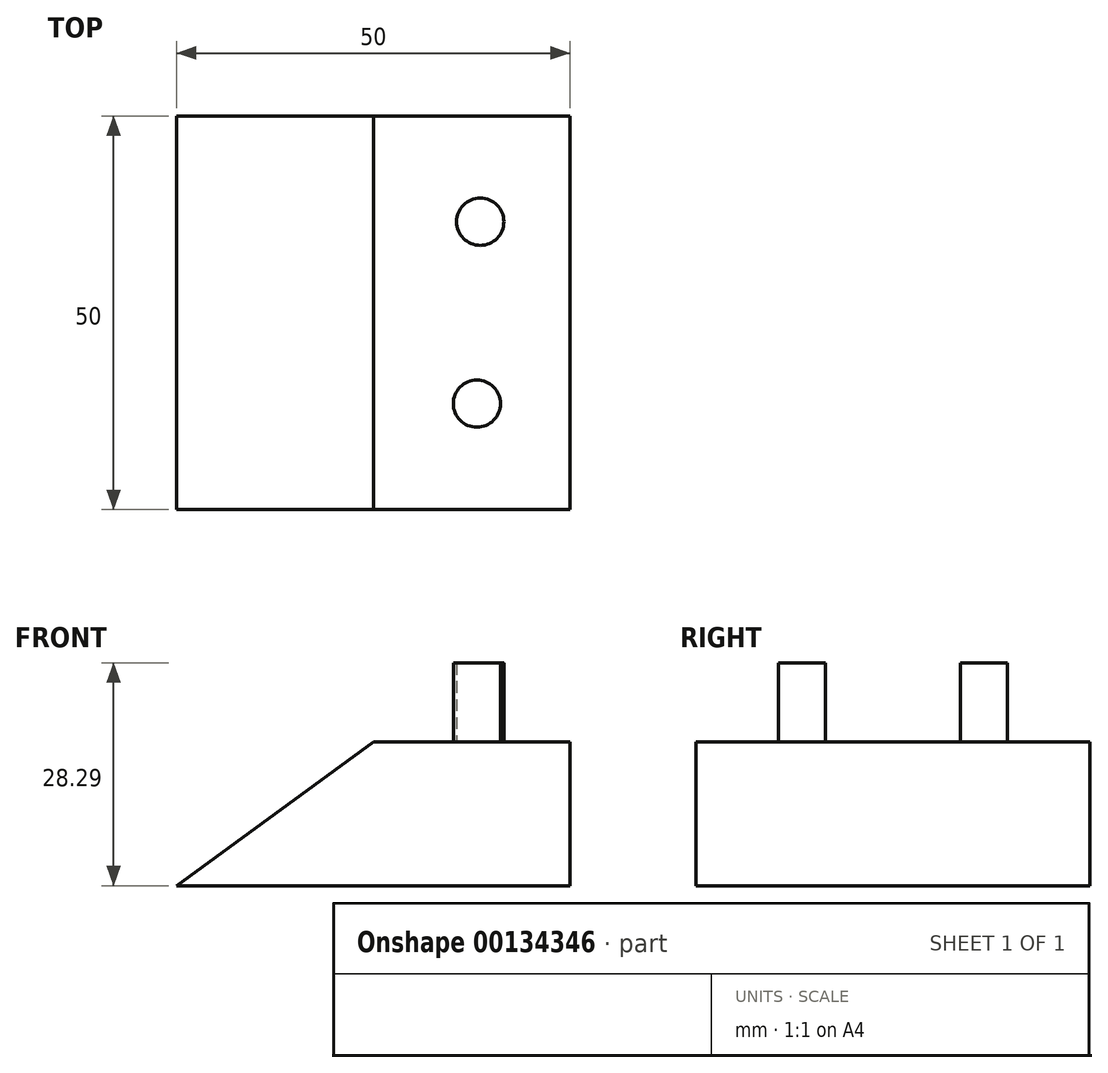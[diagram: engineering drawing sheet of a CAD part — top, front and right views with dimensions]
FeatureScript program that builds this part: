
annotation { "Feature Type Name" : "Feature", "Feature Type Description" : "" }
export const myFeature = defineFeature(function(context is Context, id is Id, definition is map)
    precondition{}
    {
        {
            var Q0;
            Q0=qCreatedBy(makeId("Front.planeOp"),FACE);
            var sketch = newSketch(context, id + "F0", { "sketchPlane" : qUnion([Q0])});
            skLineSegment(sketch, "E0", {"start": v(-25, -15.49) * mm, "end": v(25, -15.49) * mm});
            skLineSegment(sketch, "E1", {"start": v(-25, -15.49) * mm, "end": v(-25, 2.8) * mm});
            skLineSegment(sketch, "E2", {"start": v(-25, 2.8) * mm, "end": v(0, 2.8) * mm});
            skLineSegment(sketch, "E3", {"start": v(0, 2.8) * mm, "end": v(25, -15.49) * mm});
            skSolve(sketch);
        }
        {
            var Q0;
            Q0 = qSketchRegion(id + "F0", true);
            extrude(context, id + "F1", {"entities" : qUnion([Q0]), "depth" : 50 * mm});
        }
        {
            var Q0;
            Q0=makeQuery(id+"F1.opExtrude","SWEPT_FACE",FACE,{"disambiguationData":[OSD([sQuery(id+"F0.wireOp",EDGE,"E2")])]});
            var sketch = newSketch(context, id + "F2", { "sketchPlane" : qUnion([Q0])});
            skCircle(sketch, "E4", {"center": v(-13.59, -13.45) * mm, "radius": 3 * mm});
            skCircle(sketch, "E5", {"center": v(-13.16, -36.55) * mm, "radius": 3 * mm});
            skSolve(sketch);
        }
        {
            var Q0;
            Q0 = qSketchRegion(id + "F2", true);
            extrude(context, id + "F3", {"entities" : qUnion([Q0]), "operationType" : NewBodyOperationType.ADD, "depth" : 10 * mm});
        }
        {
            var Q0;
            Q0=makeQuery(id+"F1.opExtrude","SWEPT_BODY",BODY,{"disambiguationData":[OSD([sQuery(id+"F0.wireOp",EDGE,"E0"),sQuery(id+"F0.wireOp",EDGE,"E1"),sQuery(id+"F0.wireOp",EDGE,"E2"),sQuery(id+"F0.wireOp",EDGE,"E3")])]});
            var Q1;
            Q1=qCreatedBy(makeId("Right.planeOp"),FACE);
            mirror(context, id + "F4", {"entities" : qUnion([Q0]), "mirrorPlane" : qUnion([Q1])});
        }
        {
            var Q0;
            Q0=makeQuery(id+"F1.opExtrude","SWEPT_BODY",BODY,{"disambiguationData":[OSD([sQuery(id+"F0.wireOp",EDGE,"E0"),sQuery(id+"F0.wireOp",EDGE,"E1"),sQuery(id+"F0.wireOp",EDGE,"E2"),sQuery(id+"F0.wireOp",EDGE,"E3")])]});
            deleteBodies(context, id + "F5", {"entities" : qUnion([Q0])});
        }
    });
